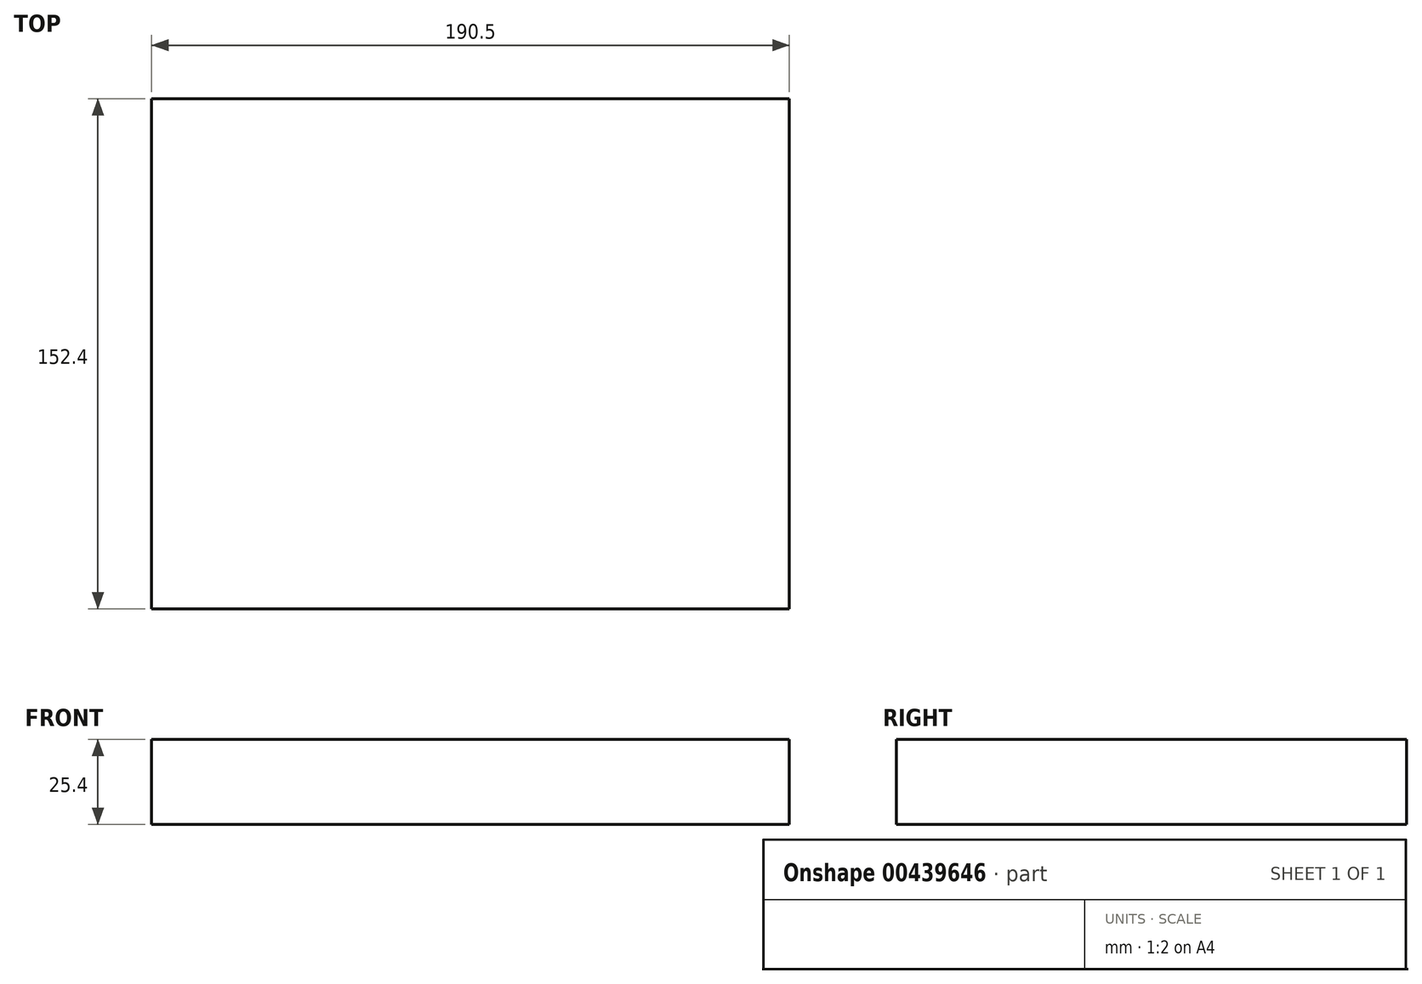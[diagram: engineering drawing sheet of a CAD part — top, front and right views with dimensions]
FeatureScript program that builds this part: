
annotation { "Feature Type Name" : "Feature", "Feature Type Description" : "" }
export const myFeature = defineFeature(function(context is Context, id is Id, definition is map)
    precondition{}
    {
        {
            var Q0;
            Q0=qCreatedBy(makeId("Top.planeOp"),FACE);
            var sketch = newSketch(context, id + "F0", { "sketchPlane" : qUnion([Q0])});
            skLineSegment(sketch, "E0.bottom", {"start": v(-95.25, 76.2) * mm, "end": v(95.25, 76.2) * mm});
            skLineSegment(sketch, "E0.top", {"start": v(-95.25, -76.2) * mm, "end": v(95.25, -76.2) * mm});
            skLineSegment(sketch, "E0.left", {"start": v(-95.25, 76.2) * mm, "end": v(-95.25, -76.2) * mm});
            skLineSegment(sketch, "E0.right", {"start": v(95.25, 76.2) * mm, "end": v(95.25, -76.2) * mm});
            skPoint(sketch, "E0.middle", {"position": v(0, 0) * mm});
            skSolve(sketch);
        }
        {
            var Q0;
            Q0 = qSketchRegion(id + "F0", true);
            extrude(context, id + "F1", {"entities" : qUnion([Q0]), "depth" : 25.4 * mm});
        }
    });
